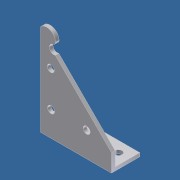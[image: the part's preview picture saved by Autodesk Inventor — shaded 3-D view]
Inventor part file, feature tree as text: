
AUTODESK INVENTOR PART (.ipt)
format: ipt  version: unknown  size: 258,048 bytes
history: native  units: in
note: dims shown in document units (in); Inventor stores cm internally (conversion verified against a paired STEP export)
features: sketch x9, plane x6, extrude x5, hole x4, fillet x1
ambient origin geometry x8: Origin, YZ Plane, XZ Plane, XY Plane, X Axis, Y Axis, Z Axis, Center Point
bodies: Solid1 (feature_tree)
feature tree (25):
  sketch  "Sketch1"  dims[d0=2.5in d1=0.125in]
  plane  "Work Plane1"
  extrude  "Extrusion2"  Depth=0.125in
  plane  "Work Plane4"
  extrude  "Extrusion3"  Depth=2.875in TaperAngle=0.0deg
  plane  "Work Plane3"
  hole  "Hole1"  [1 undecoded]
  plane  "Work Plane2"
  extrude  "Extrusion4"  Depth=0.25in
  plane  "Work Plane6"
  hole  "Hole2"  [1 undecoded]
  plane  "Work Plane5"
  hole  "Hole3"  [1 undecoded]
  extrude  "Extrusion5"  Depth=0.875in
  extrude  "Extrusion6"  Depth=1.25in
  hole  "Hole4"  [1 undecoded]
  fillet  "Fillet2"  Radius=0.375in
  sketch  "Sketch2"  dims[d4=0.125in d5=2.875in d6=0.0in]
  sketch  "Sketch3"  dims[d7=0.5in d8=45.0deg]
  sketch  "Sketch4"  dims[d9=2.875in d10=0.0in d11=0.25in]
  sketch  "Sketch5"  dims[d12=0.4687in]
  sketch  "Sketch6"  dims[d13=0.3124in d14=0.75in d15=0.375in d16=0.25in d17=0.5635in d18=1.0in d19=0.8108in d20=0.625in d21=0.2187in]
  sketch  "Sketch7"  dims[d22=0.125in d23=0.0in d25=0.375in]
  sketch  "Sketch8"  dims[d26=1.25in d27=0.875in]
  sketch  "Sketch9"  dims[d28=0.875in d29=1.25in d30=0.25in d31=0.75in d32=0.375in d33=0.25in d34=0.5635in d35=1.0in d36=0.8108in d37=0.375in d38=0.375in d39=1.25in d40=0.125in d41=0.375in d42=0.375in d43=0.25in d44=0.75in d45=0.375in d46=0.25in d47=0.5635in d48=1.0in d49=0.8108in d50=0.125in d51=0.0in d52=0.125in d53=0.875in d54=0.0in d55=0.375in d56=0.125in d57=0.375in d58=0.375in d59=0.25in d60=0.75in d61=0.375in d62=0.25in d63=0.5635in d64=1.0in d65=0.8108in d66=0.1in]
note: 4 required parameter values undecoded (feature->parameter linkage not recoverable at this tier; creation-order binding heuristic only, values carry confidence <= 0.55)
